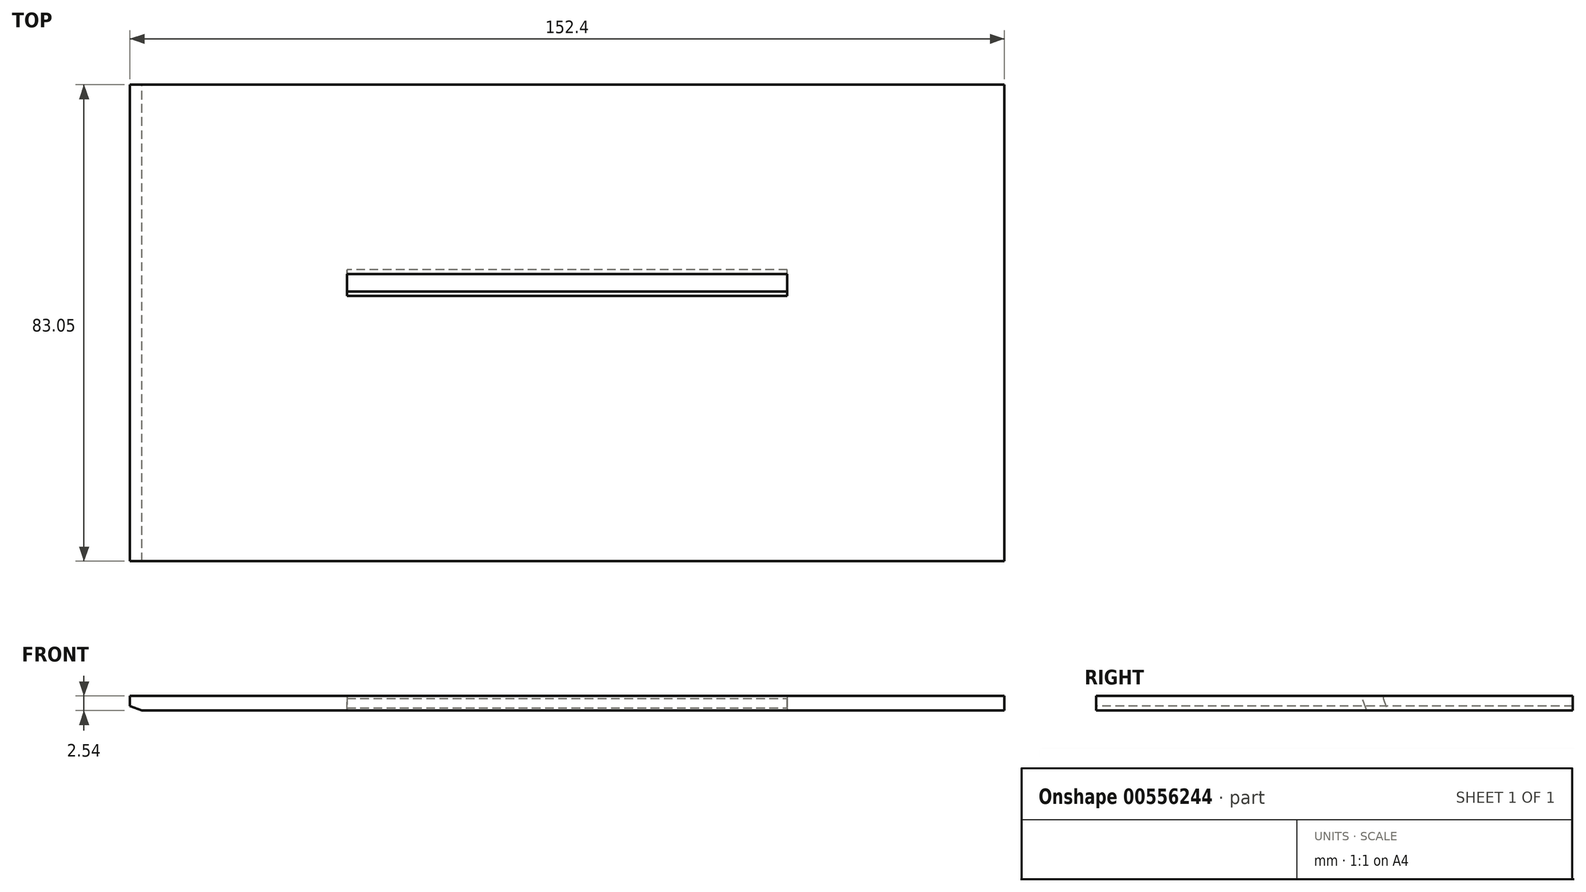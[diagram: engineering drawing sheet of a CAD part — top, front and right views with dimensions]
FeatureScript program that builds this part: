
annotation { "Feature Type Name" : "Feature", "Feature Type Description" : "" }
export const myFeature = defineFeature(function(context is Context, id is Id, definition is map)
    precondition{}
    {
        {
            var Q0;
            Q0=qCreatedBy(makeId("Top.planeOp"),FACE);
            var sketch = newSketch(context, id + "F0", { "sketchPlane" : qUnion([Q0])});
            skLineSegment(sketch, "E0.bottom", {"start": v(-76.2, 34.54) * mm, "end": v(76.2, 34.54) * mm});
            skLineSegment(sketch, "E0.top", {"start": v(-76.2, -48.51) * mm, "end": v(76.2, -48.51) * mm});
            skLineSegment(sketch, "E0.left", {"start": v(-76.2, 34.54) * mm, "end": v(-76.2, -48.51) * mm});
            skLineSegment(sketch, "E0.right", {"start": v(76.2, 34.54) * mm, "end": v(76.2, -48.51) * mm});
            skLineSegment(sketch, "E1.bottom", {"start": v(38.35, -1.52) * mm, "end": v(-38.35, -1.52) * mm});
            skLineSegment(sketch, "E1.top", {"start": v(38.35, 1.52) * mm, "end": v(-38.35, 1.52) * mm});
            skLineSegment(sketch, "E1.left", {"start": v(38.35, -1.52) * mm, "end": v(38.35, 1.52) * mm});
            skLineSegment(sketch, "E1.right", {"start": v(-38.35, -1.52) * mm, "end": v(-38.35, 1.52) * mm});
            skPoint(sketch, "E1.middle", {"position": v(0, 0) * mm});
            skSolve(sketch);
        }
        {
            var Q0;
            Q0 = qSketchRegion(id + "F0", true);
            extrude(context, id + "F1", {"entities" : qUnion([Q0]), "depth" : 2.54 * mm, "offsetDistance" : 25.4 * mm});
        }
        {
            var Q0;
            Q0=makeQuery(id+"F1.opExtrude","CAP_EDGE",EDGE,{"disambiguationData":[OSD([sQuery(id+"F0.wireOp",EDGE,"E1.top")])],"isStart":true});
            chamfer(context, id + "F2", {"entities" : qUnion([Q0]), "chamferType" : ChamferType.OFFSET_ANGLE, "width" : 0.76 * mm, "oppositeDirection" : false, "angle" : 70 * degree, "tangentPropagation" : true});
        }
        {
            var Q0;
            Q0=makeQuery(id+"F1.opExtrude","CAP_EDGE",EDGE,{"disambiguationData":[OSD([sQuery(id+"F0.wireOp",EDGE,"E1.bottom")])],"isStart":false});
            var Q1;
            Q1=makeQuery(id+"F1.opExtrude","CAP_EDGE",EDGE,{"disambiguationData":[OSD([sQuery(id+"F0.wireOp",EDGE,"E0.left")])],"isStart":true});
            chamfer(context, id + "F3", {"entities" : qUnion([Q0, Q1]), "chamferType" : ChamferType.OFFSET_ANGLE, "width" : 0.76 * mm, "oppositeDirection" : false, "angle" : 70 * degree, "tangentPropagation" : true});
        }
    });
